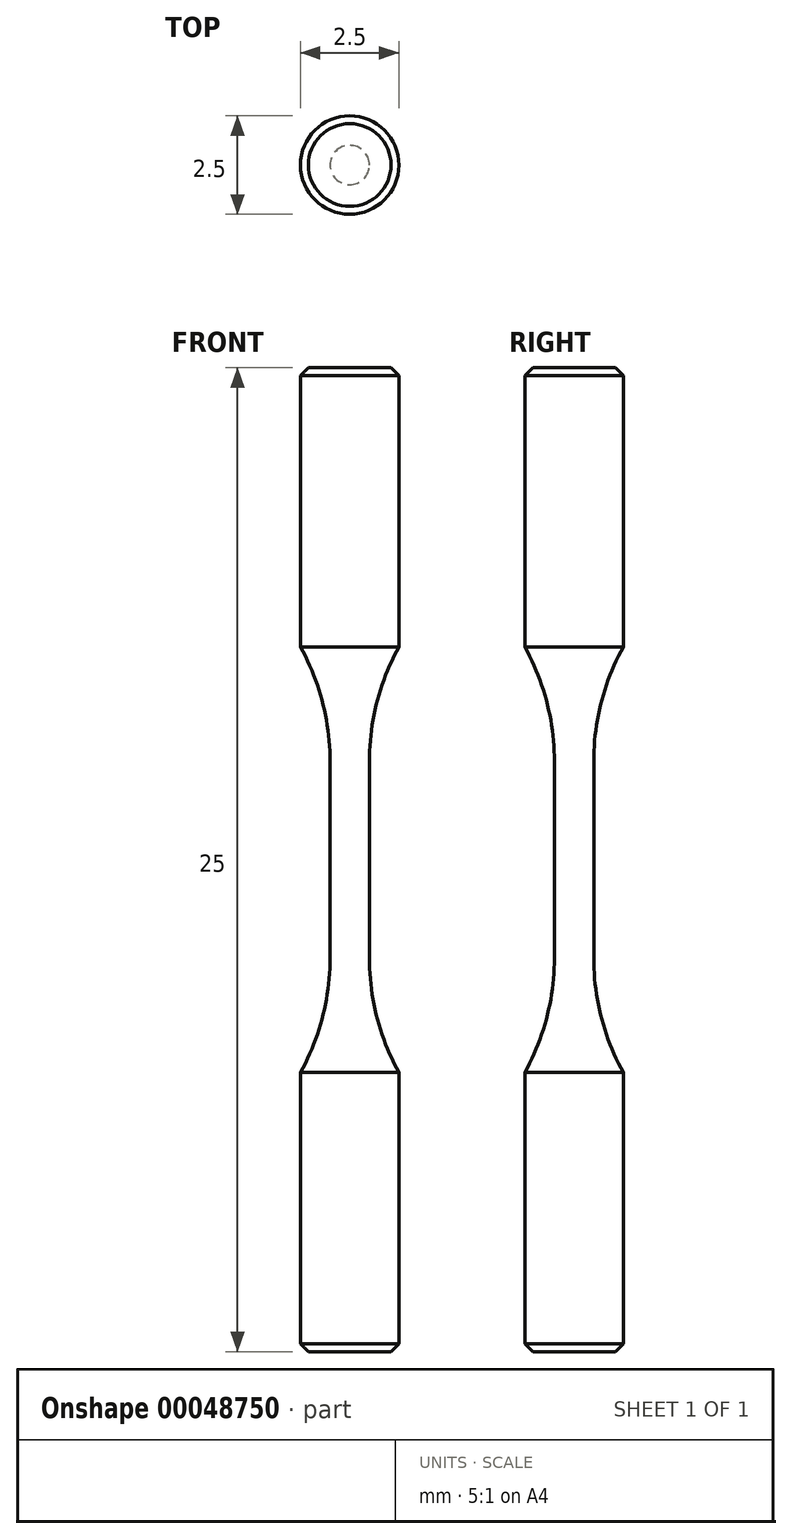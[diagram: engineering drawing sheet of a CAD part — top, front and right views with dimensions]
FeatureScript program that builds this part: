
annotation { "Feature Type Name" : "Feature", "Feature Type Description" : "" }
export const myFeature = defineFeature(function(context is Context, id is Id, definition is map)
    precondition{}
    {
        {
            var Q0;
            Q0=qCreatedBy(makeId("Front.planeOp"),FACE);
            var sketch = newSketch(context, id + "F0", { "sketchPlane" : qUnion([Q0]), "disableImprinting" : false});
            skLineSegment(sketch, "E0", {"start": v(0, 0) * mm, "end": v(0, 12.5) * mm});
            skLineSegment(sketch, "E1", {"start": v(0, 12.5) * mm, "end": v(1.25, 12.5) * mm});
            skLineSegment(sketch, "E2", {"start": v(0.5, 0) * mm, "end": v(0.5, 2.5) * mm});
            skPoint(sketch, "E3", {"position": v(6.5, 2.5) * mm});
            skLineSegment(sketch, "E4", {"start": v(1.25, 12.5) * mm, "end": v(1.25, 0) * mm, "construction": true});
            skArc(sketch, "E5", {"start": v(0.5, 2.5) * mm, "mid": v(0.7, 4) * mm, "end": v(1.25, 5.4) * mm});
            skLineSegment(sketch, "E6", {"start": v(1.25, 12.5) * mm, "end": v(1.25, 5.4) * mm});
            skLineSegment(sketch, "E7.MirrorCS", {"start": v(1.25, -12.5) * mm, "end": v(1.25, -5.4) * mm});
            skLineSegment(sketch, "E8.MirrorCS", {"start": v(0, -12.5) * mm, "end": v(1.25, -12.5) * mm});
            skLineSegment(sketch, "E9.MirrorCS", {"start": v(0.5, 0) * mm, "end": v(0.5, -2.5) * mm});
            skArc(sketch, "E10.MirrorCS", {"start": v(0.5, -2.5) * mm, "mid": v(0.7, -4) * mm, "end": v(1.25, -5.4) * mm});
            skLineSegment(sketch, "E11.MirrorCS", {"start": v(1.25, -12.5) * mm, "end": v(1.25, 0) * mm, "construction": true});
            skLineSegment(sketch, "E12.MirrorCS", {"start": v(0, 0) * mm, "end": v(0, -12.5) * mm});
            skSolve(sketch);
        }
        {
            var Q0;
            Q0=makeQuery(id+"F0.imprint","IMPRINT",FACE,{"disambiguationData":[TD([[makeQuery(id+"F0.imprint","IMPRINT",EDGE,{"derivedFrom":sQuery(id+"F0.wireOp",EDGE,"E0")}),-1.0]])]});
            var Q1;
            Q1=makeQuery(id+"F0.imprint","IMPRINT",FACE,{"disambiguationData":[TD([[makeQuery(id+"F0.imprint","IMPRINT",EDGE,{"derivedFrom":sQuery(id+"F0.wireOp",EDGE,"4tSv5JIC-juTR-nWXA-p9E0-hTueDctqZ5Lk")}),-1.0]])]});
            var Q2;
            Q2=sQuery(id+"F0.wireOp",EDGE,"E0");
            revolve(context, id + "F1", {"surfaceOperationType" : NewSurfaceOperationType.NEW, "entities" : qUnion([Q0, Q1]), "axis" : qUnion([Q2]), "revolveType" : RevolveType.FULL});
        }
        {
            var Q0;
            Q0=makeQuery(id+"F1.opRevolve","SWEPT_EDGE",EDGE,{"disambiguationData":[OSD([sQuery(id+"F0.wireOp",EDGE,"E7.MirrorCS"),sQuery(id+"F0.wireOp",EDGE,"E8.MirrorCS")])]});
            var Q1;
            Q1=makeQuery(id+"F1.opRevolve","SWEPT_EDGE",EDGE,{"disambiguationData":[OSD([sQuery(id+"F0.wireOp",EDGE,"E1"),sQuery(id+"F0.wireOp",EDGE,"E6")])]});
            chamfer(context, id + "F2", {"entities" : qUnion([Q0, Q1]), "width" : 0.2 * mm, "tangentPropagation" : true});
        }
    });
